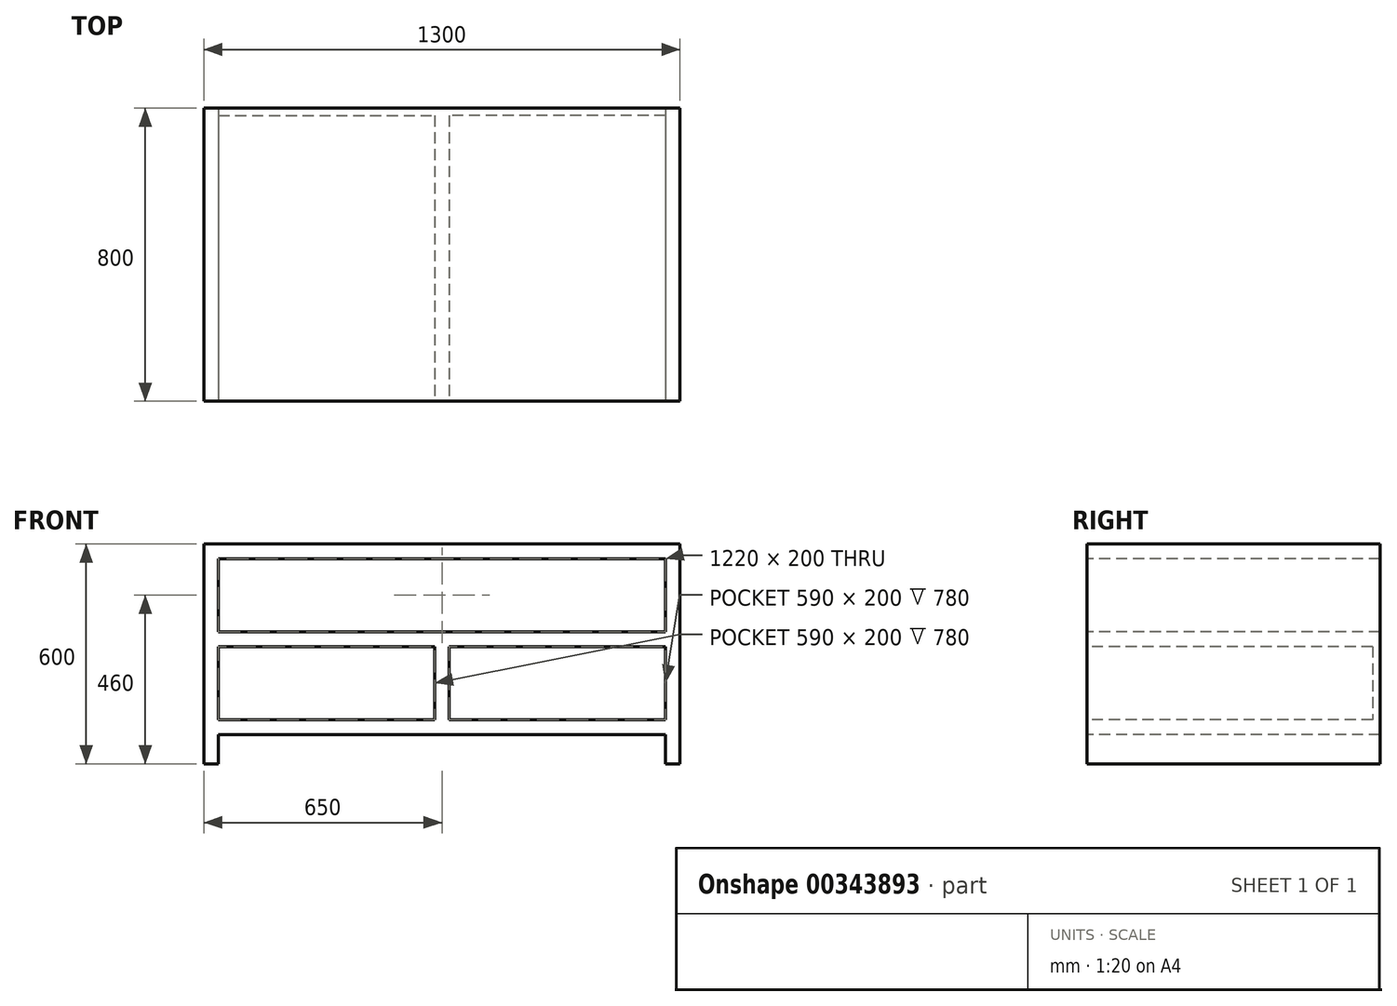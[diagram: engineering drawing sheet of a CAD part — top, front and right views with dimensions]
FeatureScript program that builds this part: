
annotation { "Feature Type Name" : "Feature", "Feature Type Description" : "" }
export const myFeature = defineFeature(function(context is Context, id is Id, definition is map)
    precondition{}
    {
        {
            var Q0;
            Q0=qCreatedBy(makeId("Front.planeOp"),FACE);
            var sketch = newSketch(context, id + "F0", { "sketchPlane" : qUnion([Q0])});
            skLineSegment(sketch, "E0.bottom", {"start": v(650, 300) * mm, "end": v(-650, 300) * mm});
            skLineSegment(sketch, "E0.top", {"start": v(650, -300) * mm, "end": v(-650, -300) * mm});
            skLineSegment(sketch, "E0.left", {"start": v(650, 300) * mm, "end": v(650, -300) * mm});
            skLineSegment(sketch, "E0.right", {"start": v(-650, 300) * mm, "end": v(-650, -300) * mm});
            skPoint(sketch, "E0.middle", {"position": v(0, 0) * mm});
            skSolve(sketch);
        }
        {
            var Q0;
            Q0 = qSketchRegion(id + "F0", true);
            extrude(context, id + "F1", {"entities" : qUnion([Q0]), "depth" : 800 * mm});
        }
        {
            var Q0;
            Q0=makeQuery(id+"F1.opExtrude","CAP_FACE",FACE,{"disambiguationData":[OSD([sQuery(id+"F0.wireOp",EDGE,"E0.bottom"),sQuery(id+"F0.wireOp",EDGE,"E0.top"),sQuery(id+"F0.wireOp",EDGE,"E0.left"),sQuery(id+"F0.wireOp",EDGE,"E0.right")])],"isStart":false});
            var sketch = newSketch(context, id + "F2", { "sketchPlane" : qUnion([Q0])});
            skLineSegment(sketch, "E1.bottom", {"start": v(-610, -300) * mm, "end": v(610, -300) * mm});
            skLineSegment(sketch, "E1.top", {"start": v(-610, -220) * mm, "end": v(610, -220) * mm});
            skLineSegment(sketch, "E1.left", {"start": v(-610, -300) * mm, "end": v(-610, -220) * mm});
            skLineSegment(sketch, "E1.right", {"start": v(610, -300) * mm, "end": v(610, -220) * mm});
            skSolve(sketch);
        }
        {
            var Q0;
            Q0 = qSketchRegion(id + "F2", true);
            extrude(context, id + "F3", {"entities" : qUnion([Q0]), "operationType" : NewBodyOperationType.REMOVE, "endBound" : BoundingType.THROUGH_ALL, "oppositeDirection" : true, "depth" : 25 * mm});
        }
        {
            var Q0;
            Q0=makeQuery(id+"F1.opExtrude","CAP_FACE",FACE,{"disambiguationData":[OSD([sQuery(id+"F0.wireOp",EDGE,"E0.bottom"),sQuery(id+"F0.wireOp",EDGE,"E0.top"),sQuery(id+"F0.wireOp",EDGE,"E0.left"),sQuery(id+"F0.wireOp",EDGE,"E0.right")])],"isStart":false});
            var sketch = newSketch(context, id + "F4", { "sketchPlane" : qUnion([Q0])});
            skLineSegment(sketch, "E2.bottom", {"start": v(-610, 260) * mm, "end": v(610, 260) * mm});
            skLineSegment(sketch, "E2.top", {"start": v(-610, 60) * mm, "end": v(610, 60) * mm});
            skLineSegment(sketch, "E2.left", {"start": v(-610, 260) * mm, "end": v(-610, 60) * mm});
            skLineSegment(sketch, "E2.right", {"start": v(610, 260) * mm, "end": v(610, 60) * mm});
            skSolve(sketch);
        }
        {
            var Q0;
            Q0=makeQuery(id+"F4.imprint","IMPRINT",FACE,{"disambiguationData":[TD([[makeQuery(id+"F4.imprint","IMPRINT",EDGE,{"derivedFrom":sQuery(id+"F4.wireOp",EDGE,"E2.bottom")}),-1.0]])]});
            extrude(context, id + "F5", {"entities" : qUnion([Q0]), "operationType" : NewBodyOperationType.REMOVE, "endBound" : BoundingType.THROUGH_ALL, "oppositeDirection" : true, "depth" : 25 * mm});
        }
        {
            var Q0;
            Q0=makeQuery(id+"F1.opExtrude","CAP_FACE",FACE,{"disambiguationData":[OSD([sQuery(id+"F0.wireOp",EDGE,"E0.bottom"),sQuery(id+"F0.wireOp",EDGE,"E0.top"),sQuery(id+"F0.wireOp",EDGE,"E0.left"),sQuery(id+"F0.wireOp",EDGE,"E0.right")])],"isStart":false});
            var sketch = newSketch(context, id + "F6", { "sketchPlane" : qUnion([Q0])});
            skLineSegment(sketch, "E3.bottom", {"start": v(-610, 20) * mm, "end": v(-20, 20) * mm});
            skLineSegment(sketch, "E3.top", {"start": v(-610, -180) * mm, "end": v(-20, -180) * mm});
            skLineSegment(sketch, "E3.left", {"start": v(-610, 20) * mm, "end": v(-610, -180) * mm});
            skLineSegment(sketch, "E3.right", {"start": v(-20, 20) * mm, "end": v(-20, -180) * mm});
            skLineSegment(sketch, "E4.MirrorCS", {"start": v(610, 20) * mm, "end": v(20, 20) * mm});
            skLineSegment(sketch, "E5.MirrorCS", {"start": v(610, -180) * mm, "end": v(20, -180) * mm});
            skLineSegment(sketch, "E6.MirrorCS", {"start": v(20, 20) * mm, "end": v(20, -180) * mm});
            skLineSegment(sketch, "E7.MirrorCS", {"start": v(610, 20) * mm, "end": v(610, -180) * mm});
            skSolve(sketch);
        }
        {
            var Q0;
            Q0=makeQuery(id+"F6.imprint","IMPRINT",FACE,{"disambiguationData":[TD([[makeQuery(id+"F6.imprint","IMPRINT",EDGE,{"derivedFrom":sQuery(id+"F6.wireOp",EDGE,"E3.bottom")}),-1.0]])]});
            var Q1;
            Q1=makeQuery(id+"F6.imprint","IMPRINT",FACE,{"disambiguationData":[TD([[makeQuery(id+"F6.imprint","IMPRINT",EDGE,{"derivedFrom":sQuery(id+"F6.wireOp",EDGE,"E4.MirrorCS")}),1.0]])]});
            extrude(context, id + "F7", {"entities" : qUnion([Q0, Q1]), "operationType" : NewBodyOperationType.REMOVE, "oppositeDirection" : true, "depth" : 780 * mm});
        }
    });
